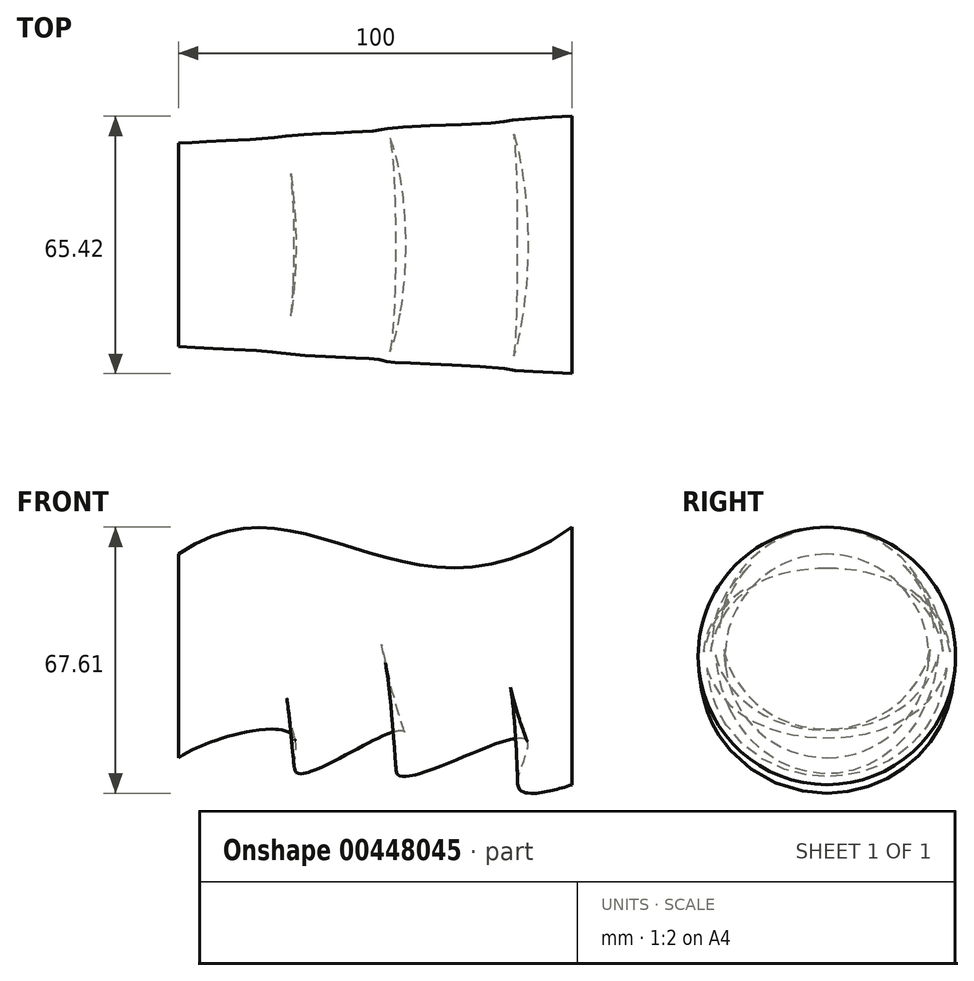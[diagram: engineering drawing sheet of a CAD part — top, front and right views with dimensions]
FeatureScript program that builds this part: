
annotation { "Feature Type Name" : "Feature", "Feature Type Description" : "" }
export const myFeature = defineFeature(function(context is Context, id is Id, definition is map)
    precondition{}
    {
        {
            var Q0;
            Q0=qCreatedBy(makeId("Right.planeOp"),FACE);
            cPlane(context, id + "F0", {"entities" : qUnion([Q0]), "cplaneType" : CPlaneType.OFFSET, "offset" : 50 * mm, "width" : 150 * mm, "height" : 150 * mm});
        }
        {
            var Q0;
            Q0=qCreatedBy(makeId("Right.planeOp"),FACE);
            cPlane(context, id + "F1", {"entities" : qUnion([Q0]), "cplaneType" : CPlaneType.OFFSET, "offset" : 50 * mm, "oppositeDirection" : true, "width" : 150 * mm, "height" : 150 * mm});
        }
        {
            var Q0;
            Q0=qCreatedBy(id+"F0.planeOp",FACE);
            var sketch = newSketch(context, id + "F2", { "sketchPlane" : qUnion([Q0])});
            skCircle(sketch, "E0", {"center": v(0, 0) * mm, "radius": 32.7 * mm});
            skSolve(sketch);
        }
        {
            var Q0;
            Q0=qCreatedBy(id+"F1.planeOp",FACE);
            var sketch = newSketch(context, id + "F3", { "sketchPlane" : qUnion([Q0])});
            skCircle(sketch, "E1", {"center": v(0, 0) * mm, "radius": 25.86 * mm});
            skSolve(sketch);
        }
        {
            var Q0;
            Q0=qCreatedBy(makeId("Front.planeOp"),FACE);
            var sketch = newSketch(context, id + "F4", { "sketchPlane" : qUnion([Q0])});
            skLineSegment(sketch, "E2.0", {"start": v(-50, 25.86) * mm, "end": v(-50, -25.86) * mm});
            skLineSegment(sketch, "E3.0", {"start": v(50, 32.7) * mm, "end": v(50, -32.7) * mm});
            skFitSpline(sketch, "E4", {"points": [v(-50, 25.86) * mm, v(50, 32.7) * mm], "startDerivative": vector(97.6, 68.9) * mm, "endDerivative": vector(126.08, 88.68) * mm});
            skFitSpline(sketch, "E5", {"points": [v(-50, -25.86) * mm, v(-20.94, -20.2) * mm, v(-19.75, -29.84) * mm, v(7.3, -19.15) * mm, v(5.7, -30.18) * mm, v(38.1, -21.08) * mm, v(36.29, -33.27) * mm, v(50, -32.7) * mm], "startDerivative": vector(89.73, 68.16) * mm, "endDerivative": vector(116.05, 39.26) * mm});
            skSolve(sketch);
        }
        {
            var Q0;
            Q0=makeQuery(id+"F3.imprint","IMPRINT",FACE,{"disambiguationData":[TD([[makeQuery(id+"F3.imprint","IMPRINT",EDGE,{"derivedFrom":sQuery(id+"F3.wireOp",EDGE,"E1")}),1.0]])]});
            var Q1;
            Q1=makeQuery(id+"F2.imprint","IMPRINT",FACE,{"disambiguationData":[TD([[makeQuery(id+"F2.imprint","IMPRINT",EDGE,{"derivedFrom":sQuery(id+"F2.wireOp",EDGE,"E0")}),1.0]])]});
            var Q2;
            Q2=sQuery(id+"F4.wireOp",EDGE,"E4");
            var Q3;
            Q3=sQuery(id+"F4.wireOp",EDGE,"E5");
            loft(context, id + "F5", {"addGuides" : true, "sheetProfilesArray" : [{ "sheetProfileEntities" : qUnion([Q0]) }, { "sheetProfileEntities" : qUnion([Q1]) }], "guidesArray" : [{ "guideEntities" : qUnion([Q2]), "guideDerivativeType" : LoftGuideDerivativeType.DEFAULT, "guideDerivativeMagnitude" : 1 }, { "guideEntities" : qUnion([Q3]), "guideDerivativeType" : LoftGuideDerivativeType.DEFAULT, "guideDerivativeMagnitude" : 1 }]});
        }
    });
